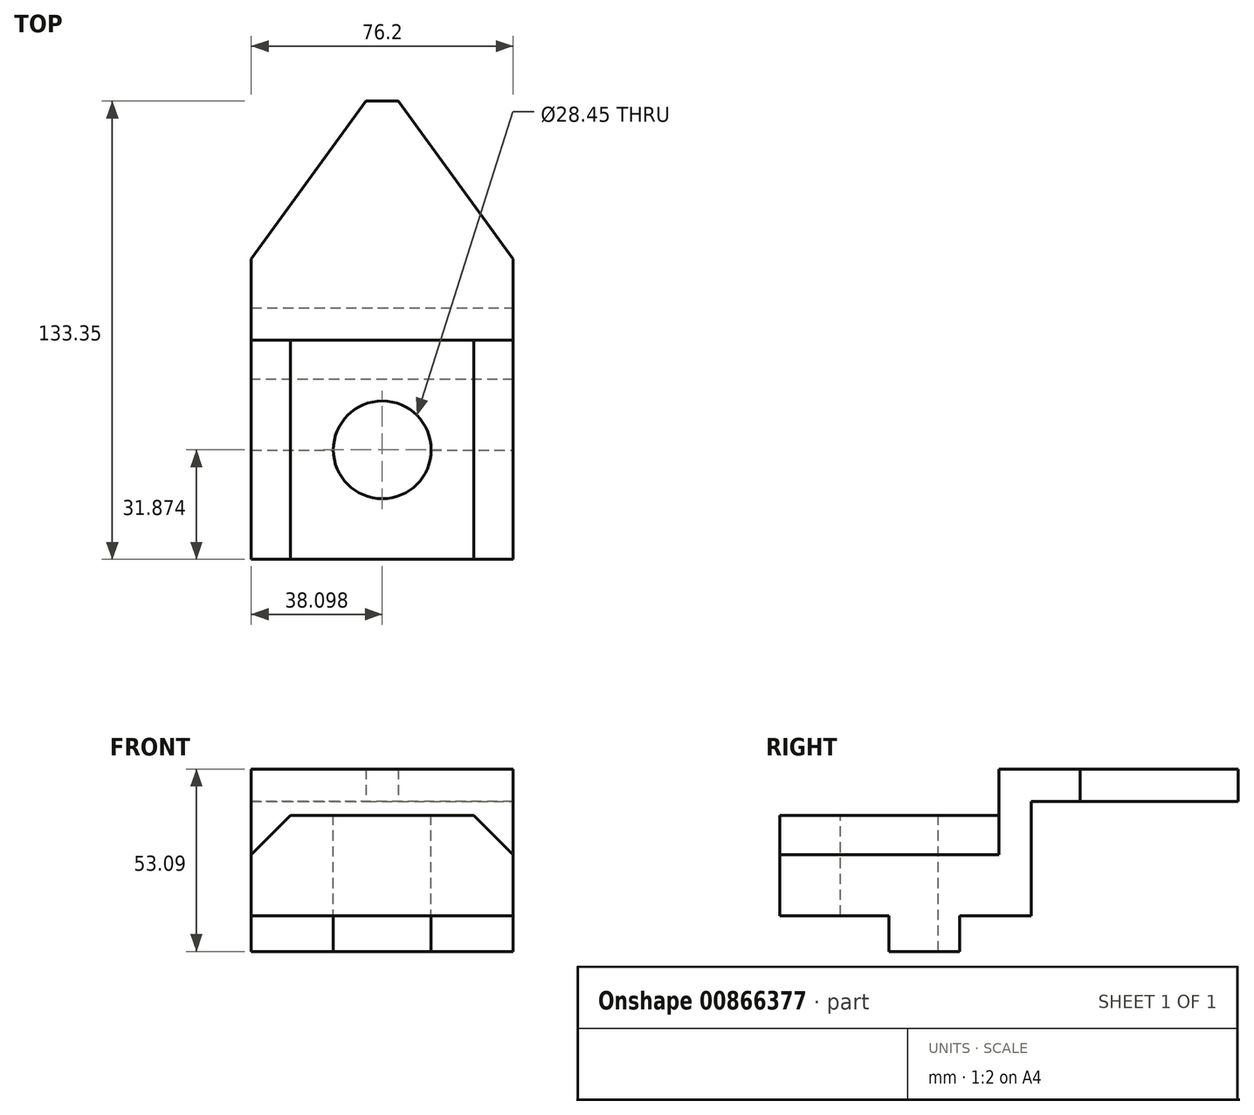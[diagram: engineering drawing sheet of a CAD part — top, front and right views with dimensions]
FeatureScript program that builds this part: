
annotation { "Feature Type Name" : "Feature", "Feature Type Description" : "" }
export const myFeature = defineFeature(function(context is Context, id is Id, definition is map)
    precondition{}
    {
        {
            var Q0;
            Q0=qCreatedBy(makeId("Top.planeOp"),FACE);
            var sketch = newSketch(context, id + "F0", { "sketchPlane" : qUnion([Q0])});
            skLineSegment(sketch, "E0", {"start": v(-49.31, -9.92) * mm, "end": v(-49.31, 13.7) * mm});
            skLineSegment(sketch, "E1", {"start": v(-49.31, 13.7) * mm, "end": v(-15.91, 59.68) * mm});
            skLineSegment(sketch, "E2", {"start": v(-15.91, 59.68) * mm, "end": v(-6.51, 59.68) * mm});
            skLineSegment(sketch, "E3", {"start": v(-6.51, 59.68) * mm, "end": v(26.89, 13.7) * mm});
            skLineSegment(sketch, "E4", {"start": v(26.89, 13.7) * mm, "end": v(26.89, -9.92) * mm});
            skLineSegment(sketch, "E5", {"start": v(26.89, -9.92) * mm, "end": v(-49.31, -9.92) * mm});
            skSolve(sketch);
        }
        {
            var Q0;
            Q0=makeQuery(id+"F0.imprint","IMPRINT",FACE,{"disambiguationData":[TD([[makeQuery(id+"F0.imprint","IMPRINT",EDGE,{"derivedFrom":sQuery(id+"F0.wireOp",EDGE,"E0")}),-1.0]])]});
            extrude(context, id + "F1", {"entities" : qUnion([Q0]), "depth" : 9.4 * mm, "offsetDistance" : 25.4 * mm});
        }
        {
            var Q0;
            Q0=makeQuery(id+"F1.opExtrude","SWEPT_FACE",FACE,{"disambiguationData":[OSD([sQuery(id+"F0.wireOp",EDGE,"E5")])]});
            var sketch = newSketch(context, id + "F2", { "sketchPlane" : qUnion([Q0])});
            skLineSegment(sketch, "E6", {"start": v(-49.31, 0) * mm, "end": v(-49.31, -33.27) * mm});
            skLineSegment(sketch, "E7", {"start": v(-49.31, -33.27) * mm, "end": v(26.89, -33.27) * mm});
            skLineSegment(sketch, "E8", {"start": v(26.89, -33.27) * mm, "end": v(26.89, 0) * mm});
            skSolve(sketch);
        }
        {
            var Q0;
            Q0=makeQuery(id+"F2.imprint","IMPRINT",FACE,{"disambiguationData":[TD([[makeQuery(id+"F2.imprint","IMPRINT",EDGE,{"derivedFrom":sQuery(id+"F2.wireOp",EDGE,"E6")}),1.0]])]});
            extrude(context, id + "F3", {"entities" : qUnion([Q0]), "operationType" : NewBodyOperationType.ADD, "oppositeDirection" : true, "depth" : 9.4 * mm, "offsetDistance" : 25.4 * mm});
        }
        {
            var Q0;
            {var subQ0=sQuery(id+"F0.wireOp",EDGE,"E5");Q0=makeQuery(id+"F3.boolean.opBoolean","MERGE",FACE,{"derivedFrom":[makeQuery(id+"F1.opExtrude","SWEPT_FACE",FACE,{"disambiguationData":[OSD([subQ0])]}),makeQuery(id+"F3.opExtrude","CAP_FACE",FACE,{"disambiguationData":[OSD([subQ0,sQuery(id+"F2.wireOp",EDGE,"E6"),sQuery(id+"F2.wireOp",EDGE,"E7"),sQuery(id+"F2.wireOp",EDGE,"E8")])],"isStart":true})]});}
            var sketch = newSketch(context, id + "F4", { "sketchPlane" : qUnion([Q0])});
            skLineSegment(sketch, "E9", {"start": v(-49.31, -4.07) * mm, "end": v(26.89, -4.07) * mm});
            skSolve(sketch);
        }
        {
            var Q0;
            {var subQ0=sQuery(id+"F4.wireOp",EDGE,"E9");Q0=makeQuery(id+"F4.imprint","IMPRINT",FACE,{"disambiguationData":[TD([[makeQuery(id+"F4.imprint","IMPRINT",EDGE,{"derivedFrom":subQ0}),-1.0]])]});}
            extrude(context, id + "F5", {"entities" : qUnion([Q0]), "operationType" : NewBodyOperationType.ADD, "depth" : 63.75 * mm, "offsetDistance" : 25.4 * mm});
        }
        {
            var Q0;
            Q0=makeQuery(id+"F5.opExtrude","SWEPT_EDGE",EDGE,{"disambiguationData":[OSD([sQuery(id+"F0.wireOp",EDGE,"E4"),sQuery(id+"F0.wireOp",EDGE,"E5"),sQuery(id+"F2.wireOp",EDGE,"E8"),sQuery(id+"F4.wireOp",EDGE,"E9")])]});
            var Q1;
            Q1=makeQuery(id+"F5.opExtrude","SWEPT_EDGE",EDGE,{"disambiguationData":[OSD([sQuery(id+"F0.wireOp",EDGE,"E0"),sQuery(id+"F0.wireOp",EDGE,"E5"),sQuery(id+"F2.wireOp",EDGE,"E6"),sQuery(id+"F4.wireOp",EDGE,"E9")])]});
            chamfer(context, id + "F6", {"entities" : qUnion([Q0, Q1]), "width" : 11.43 * mm, "tangentPropagation" : true});
        }
        {
            var Q0;
            {var subQ0=sQuery(id+"F2.wireOp",EDGE,"E7");Q0=makeQuery(id+"F5.boolean.opBoolean","MERGE",FACE,{"derivedFrom":[makeQuery(id+"F3.opExtrude","SWEPT_FACE",FACE,{"disambiguationData":[OSD([subQ0])]}),makeQuery(id+"F5.opExtrude","SWEPT_FACE",FACE,{"disambiguationData":[OSD([subQ0])]})]});}
            var sketch = newSketch(context, id + "F7", { "sketchPlane" : qUnion([Q0])});
            skLineSegment(sketch, "E10", {"start": v(-49.31, 41.92) * mm, "end": v(26.89, 41.92) * mm});
            skLineSegment(sketch, "E11", {"start": v(26.89, 41.92) * mm, "end": v(26.89, 21.35) * mm});
            skLineSegment(sketch, "E12", {"start": v(26.89, 21.35) * mm, "end": v(-49.31, 21.35) * mm});
            skSolve(sketch);
        }
        {
            var Q0;
            {var subQ0=sQuery(id+"F7.wireOp",EDGE,"E10");Q0=makeQuery(id+"F7.imprint","IMPRINT",FACE,{"disambiguationData":[TD([[makeQuery(id+"F7.imprint","IMPRINT",EDGE,{"derivedFrom":subQ0}),-1.0]])]});}
            extrude(context, id + "F8", {"entities" : qUnion([Q0]), "operationType" : NewBodyOperationType.ADD, "depth" : 10.4 * mm, "offsetDistance" : 25.4 * mm});
        }
        {
            var Q0;
            Q0=makeQuery(id+"F5.opExtrude","SWEPT_FACE",FACE,{"disambiguationData":[OSD([sQuery(id+"F4.wireOp",EDGE,"E9")])]});
            var sketch = newSketch(context, id + "F9", { "sketchPlane" : qUnion([Q0])});
            skCircle(sketch, "E13", {"center": v(-11.21, -41.8) * mm, "radius": 14.22 * mm});
            skPoint(sketch, "E13.centerSnap0", {"position": v(-11.21, -73.67) * mm});
            skPoint(sketch, "E13.centerSnap1", {"position": v(-37.88, -41.8) * mm});
            skSolve(sketch);
        }
        {
            var Q0;
            Q0=makeQuery(id+"F9.imprint","IMPRINT",FACE,{"disambiguationData":[TD([[makeQuery(id+"F9.imprint","IMPRINT",EDGE,{"derivedFrom":sQuery(id+"F9.wireOp",EDGE,"E13")}),1.0]])]});
            extrude(context, id + "F10", {"entities" : qUnion([Q0]), "operationType" : NewBodyOperationType.REMOVE, "oppositeDirection" : true, "depth" : 221.5 * mm, "offsetDistance" : 25.4 * mm});
        }
    });
